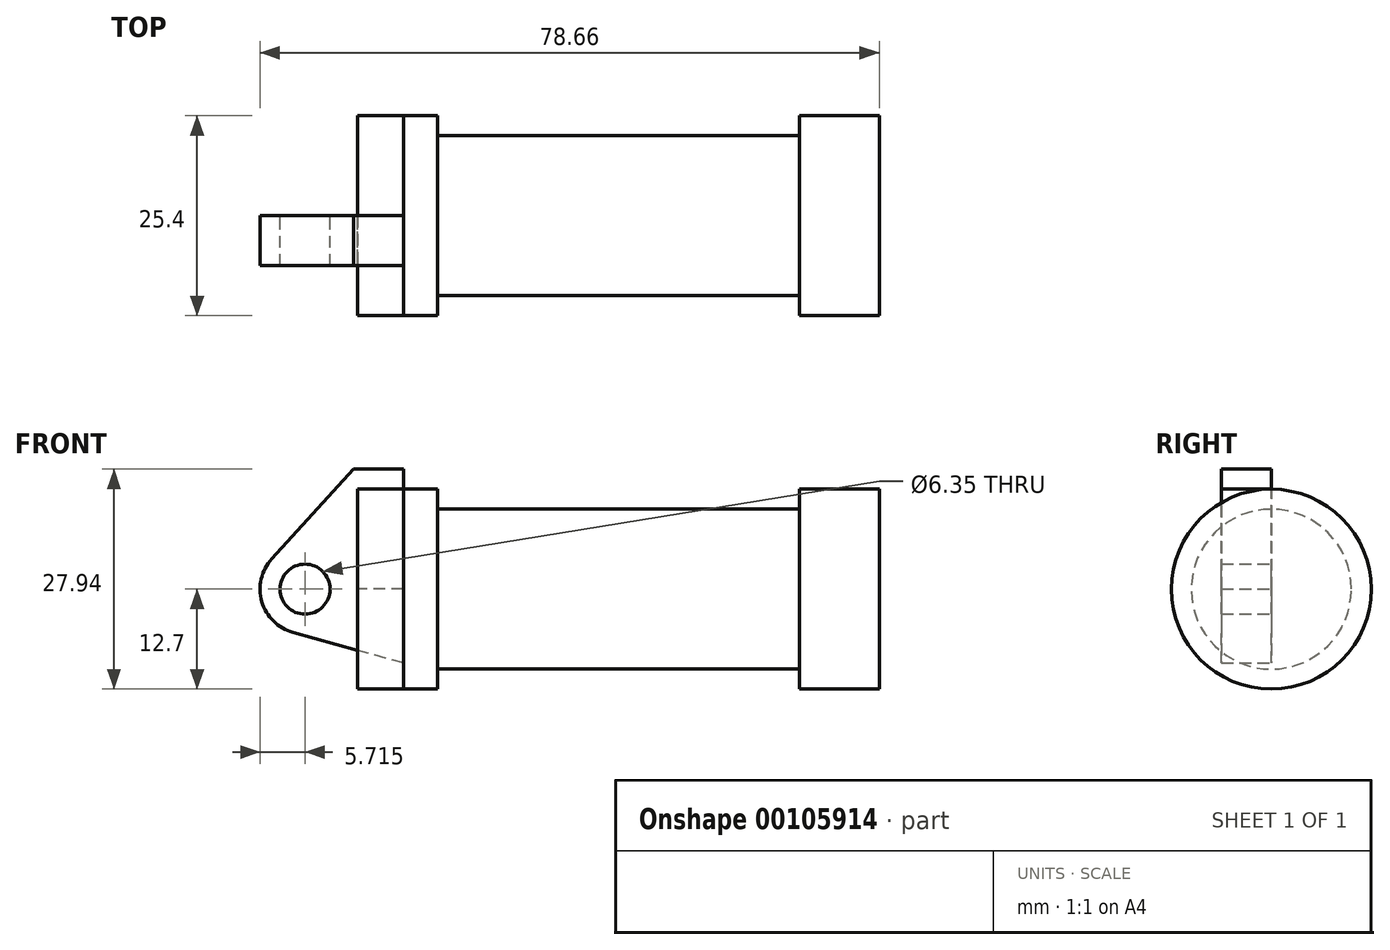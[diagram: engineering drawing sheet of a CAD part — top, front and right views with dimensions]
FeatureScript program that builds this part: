
annotation { "Feature Type Name" : "Feature", "Feature Type Description" : "" }
export const myFeature = defineFeature(function(context is Context, id is Id, definition is map)
    precondition{}
    {
        {
            var Q0;
            Q0=qCreatedBy(makeId("Front.planeOp"),FACE);
            var sketch = newSketch(context, id + "F0", { "sketchPlane" : qUnion([Q0])});
            skLineSegment(sketch, "E0", {"start": v(0, 0) * mm, "end": v(0, 12.7) * mm});
            skLineSegment(sketch, "E1", {"start": v(0, 12.7) * mm, "end": v(10.16, 12.7) * mm});
            skLineSegment(sketch, "E2", {"start": v(10.16, 12.7) * mm, "end": v(10.16, 10.16) * mm});
            skLineSegment(sketch, "E3", {"start": v(10.16, 10.16) * mm, "end": v(56.13, 10.16) * mm});
            skLineSegment(sketch, "E4", {"start": v(56.13, 10.16) * mm, "end": v(56.13, 12.7) * mm});
            skLineSegment(sketch, "E5", {"start": v(56.13, 12.7) * mm, "end": v(66.3, 12.7) * mm});
            skLineSegment(sketch, "E6", {"start": v(66.3, 12.7) * mm, "end": v(66.3, 0) * mm});
            skLineSegment(sketch, "E7", {"start": v(66.3, 0) * mm, "end": v(0, 0) * mm});
            skLineSegment(sketch, "E8", {"start": v(5.84, 15.24) * mm, "end": v(-0.5, 15.24) * mm});
            skLineSegment(sketch, "E9", {"start": v(-0.5, 15.24) * mm, "end": v(-10.88, 3.85) * mm});
            skLineSegment(sketch, "E10", {"start": v(0, 0) * mm, "end": v(-6.65, 0) * mm});
            skCircle(sketch, "E11", {"center": v(-6.65, 0) * mm, "radius": 5.72 * mm});
            skCircle(sketch, "E12", {"center": v(-6.65, 0) * mm, "radius": 3.18 * mm});
            skLineSegment(sketch, "E13", {"start": v(5.84, 15.24) * mm, "end": v(5.84, -9.4) * mm});
            skLineSegment(sketch, "E14", {"start": v(5.84, -9.4) * mm, "end": v(-8.18, -5.5) * mm});
            skSolve(sketch);
        }
        {
            var Q0;
            {var subQ0=sQuery(id+"F0.wireOp",EDGE,"E2");Q0=makeQuery(id+"F0.imprint","IMPRINT",FACE,{"disambiguationData":[TD([[makeQuery(id+"F0.imprint","IMPRINT",EDGE,{"derivedFrom":subQ0}),-1.0]])]});}
            var Q1;
            Q1=sQuery(id+"F0.wireOp",EDGE,"E7");
            revolve(context, id + "F1", {"entities" : qUnion([Q0]), "axis" : qUnion([Q1]), "revolveType" : RevolveType.FULL});
        }
        {
            var Q0;
            {var subQ3=sQuery(id+"F0.wireOp",EDGE,"E0");Q0=makeQuery(id+"F0.imprint","IMPRINT",FACE,{"disambiguationData":[TD([[makeQuery(id+"F0.imprint","IMPRINT",EDGE,{"derivedFrom":subQ3}),1.0]])]});}
            var Q1;
            {var subQ4=sQuery(id+"F0.wireOp",EDGE,"E12");Q1=makeQuery(id+"F0.imprint","IMPRINT",FACE,{"disambiguationData":[TD([[makeQuery(id+"F0.imprint","IMPRINT",EDGE,{"derivedFrom":subQ4}),-1.0]])]});}
            var Q2;
            {var subQ0=sQuery(id+"F0.wireOp",EDGE,"E14");Q2=makeQuery(id+"F0.imprint","IMPRINT",FACE,{"disambiguationData":[TD([[makeQuery(id+"F0.imprint","IMPRINT",EDGE,{"derivedFrom":subQ0}),-1.0]])]});}
            extrude(context, id + "F2", {"entities" : qUnion([Q0, Q1, Q2]), "depth" : 6.35 * mm});
        }
        {
            var Q0;
            {var subQ0=sQuery(id+"F0.wireOp",EDGE,"E0");Q0=makeQuery(id+"F0.imprint","IMPRINT",FACE,{"disambiguationData":[TD([[makeQuery(id+"F0.imprint","IMPRINT",EDGE,{"derivedFrom":subQ0}),-1.0]])]});}
            var Q1;
            Q1=sQuery(id+"F0.wireOp",EDGE,"E7");
            revolve(context, id + "F3", {"entities" : qUnion([Q0]), "axis" : qUnion([Q1]), "revolveType" : RevolveType.FULL});
        }
    });
